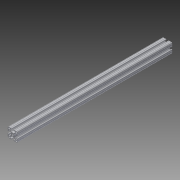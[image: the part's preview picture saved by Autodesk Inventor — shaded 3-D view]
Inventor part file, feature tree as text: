
AUTODESK INVENTOR PART (.ipt)
format: ipt  version: 2013 (Build 170138000, 138)  size: 292,352 bytes
history: native  units: in
note: dims shown in document units (in); Inventor stores cm internally (conversion verified against a paired STEP export)
features: extrude x1, sketch x1
ambient origin geometry x8: Origin, YZ Plane, XZ Plane, XY Plane, X Axis, Y Axis, Z Axis, Center Point
bodies: Solid1 (feature_tree)
feature tree (2):
  extrude  "Extrusion1"  [1 undecoded]
  sketch  "Sketch1"  dims[d0=24.0in d1=0.0in]
note: 1 required parameter value undecoded (feature->parameter linkage not recoverable at this tier; creation-order binding heuristic only, values carry confidence <= 0.55)
